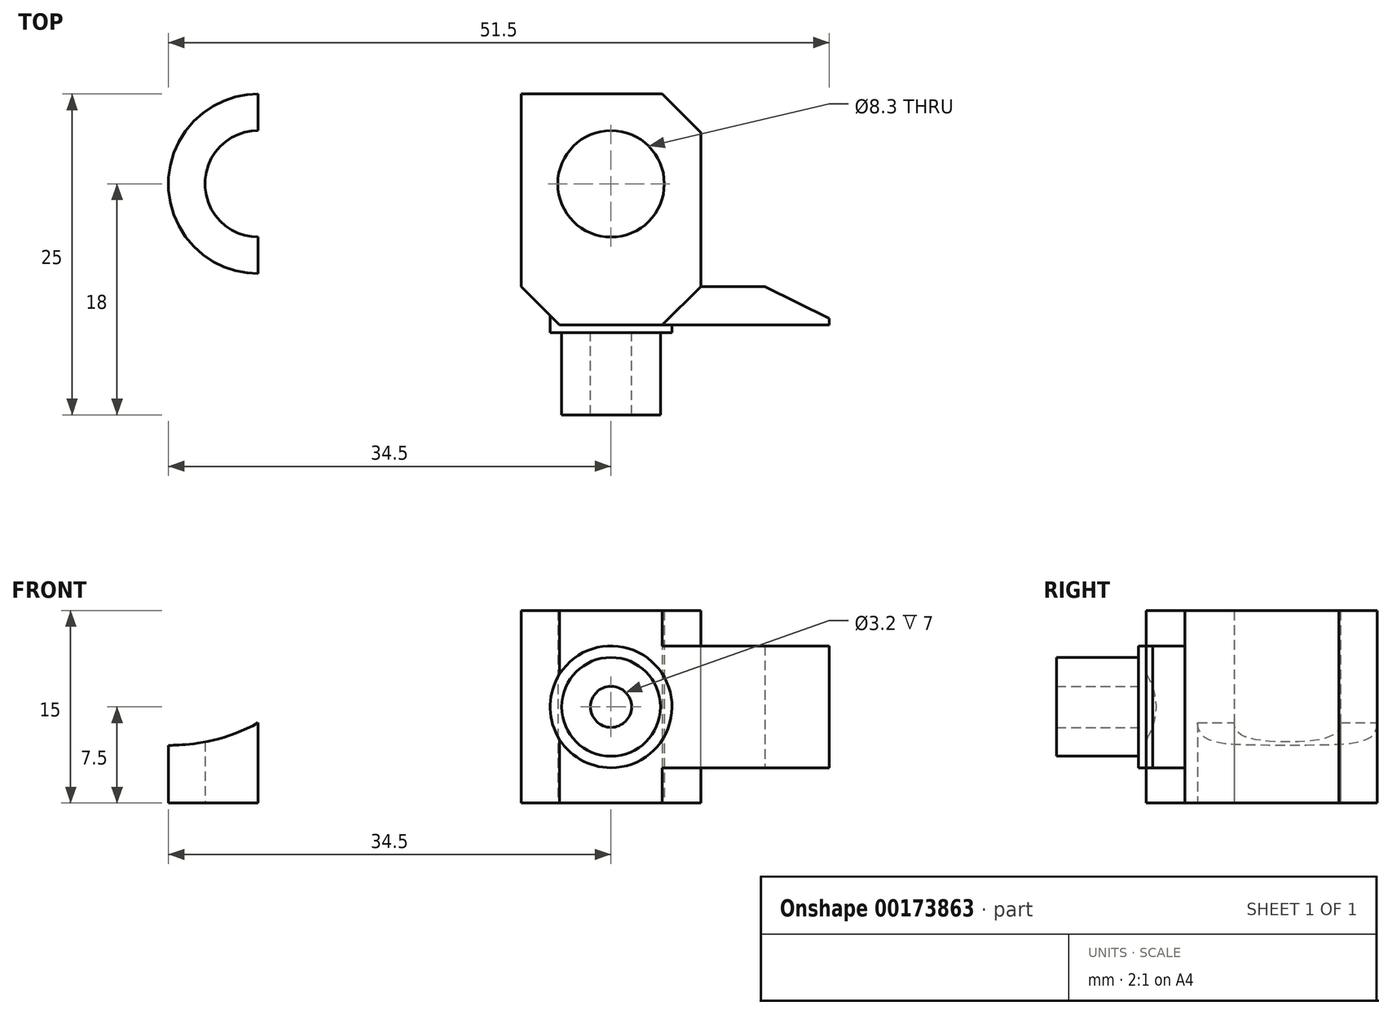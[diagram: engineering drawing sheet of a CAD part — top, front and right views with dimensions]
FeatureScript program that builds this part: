
annotation { "Feature Type Name" : "Feature", "Feature Type Description" : "" }
export const myFeature = defineFeature(function(context is Context, id is Id, definition is map)
    precondition{}
    {
        {
            var Q0;
            Q0=qCreatedBy(makeId("Top.planeOp"),FACE);
            var sketch = newSketch(context, id + "F0", { "sketchPlane" : qUnion([Q0])});
            skCircle(sketch, "E0", {"center": v(0, 0) * mm, "radius": 4.15 * mm});
            skLineSegment(sketch, "E1", {"start": v(0, 0) * mm, "end": v(-27.5, 0) * mm, "construction": true});
            skCircle(sketch, "E2", {"center": v(-27.5, 0) * mm, "radius": 4.15 * mm});
            skArc(sketch, "E3", {"start": v(-27.5, 7) * mm, "mid": v(-34.5, 0) * mm, "end": v(-27.5, -7) * mm});
            skLineSegment(sketch, "E4", {"start": v(-27.5, -7) * mm, "end": v(7, -7) * mm});
            skLineSegment(sketch, "E5", {"start": v(7, -7) * mm, "end": v(7, 7) * mm});
            skLineSegment(sketch, "E6", {"start": v(-27.5, 7) * mm, "end": v(7, 7) * mm});
            skSolve(sketch);
        }
        {
            var Q0;
            Q0=makeQuery(id+"F0.imprint","IMPRINT",FACE,{"disambiguationData":[TD([[makeQuery(id+"F0.imprint","IMPRINT",EDGE,{"derivedFrom":sQuery(id+"F0.wireOp",EDGE,"E0")}),-1.0]])]});
            extrude(context, id + "F1", {"entities" : qUnion([Q0]), "depth" : 15 * mm});
        }
        {
            var Q0;
            Q0=makeQuery(id+"F1.opExtrude","SWEPT_FACE",FACE,{"disambiguationData":[OSD([sQuery(id+"F0.wireOp",EDGE,"E4")])]});
            var sketch = newSketch(context, id + "F2", { "sketchPlane" : qUnion([Q0])});
            skLineSegment(sketch, "E7", {"start": v(-7, 15) * mm, "end": v(-7, 0) * mm});
            skSolve(sketch);
        }
        {
            var Q0;
            {var subQ0=sQuery(id+"F2.wireOp",EDGE,"E7");Q0=makeQuery(id+"F2.imprint","IMPRINT",FACE,{"disambiguationData":[TD([[makeQuery(id+"F2.imprint","IMPRINT",EDGE,{"derivedFrom":subQ0}),1.0]])]});}
            extrude(context, id + "F3", {"entities" : qUnion([Q0]), "operationType" : NewBodyOperationType.ADD, "depth" : 4 * mm});
        }
        {
            var Q0;
            Q0=makeQuery(id+"F3.opExtrude","CAP_FACE",FACE,{"disambiguationData":[OSD([sQuery(id+"F0.wireOp",EDGE,"E4"),sQuery(id+"F0.wireOp",EDGE,"E5"),sQuery(id+"F2.wireOp",EDGE,"E7")])],"isStart":false});
            var sketch = newSketch(context, id + "F4", { "sketchPlane" : qUnion([Q0])});
            skCircle(sketch, "E8", {"center": v(0, 7.5) * mm, "radius": 3.85 * mm});
            skCircle(sketch, "E9", {"center": v(0, 7.5) * mm, "radius": 1.6 * mm});
            skCircle(sketch, "E10", {"center": v(0, 7.5) * mm, "radius": 4.75 * mm});
            skPoint(sketch, "E11.positionSnap0", {"position": v(0, 15) * mm});
            skPoint(sketch, "E11.positionSnap1", {"position": v(7, 7.5) * mm});
            skLineSegment(sketch, "E12", {"start": v(0, 12.25) * mm, "end": v(-18, 12.25) * mm});
            skLineSegment(sketch, "E13", {"start": v(-18, 12.25) * mm, "end": v(-18, 2.75) * mm});
            skLineSegment(sketch, "E14", {"start": v(-18, 2.75) * mm, "end": v(0, 2.75) * mm});
            skLineSegment(sketch, "E15", {"start": v(0, 2.75) * mm, "end": v(18, 2.75) * mm});
            skLineSegment(sketch, "E16", {"start": v(18, 2.75) * mm, "end": v(18, 12.25) * mm});
            skLineSegment(sketch, "E17", {"start": v(18, 12.25) * mm, "end": v(0, 12.25) * mm});
            skSolve(sketch);
        }
        {
            var Q0;
            Q0 = qSketchRegion(id + "F4", true);
            extrude(context, id + "F5", {"entities" : qUnion([Q0]), "operationType" : NewBodyOperationType.ADD, "oppositeDirection" : true, "depth" : 3 * mm});
        }
        {
            var Q0;
            Q0=makeQuery(id+"F5.opExtrude","CAP_EDGE",EDGE,{"disambiguationData":[OSD([sQuery(id+"F4.wireOp",EDGE,"E13")])],"isStart":false});
            var Q1;
            Q1=makeQuery(id+"F5.opExtrude","CAP_EDGE",EDGE,{"disambiguationData":[OSD([sQuery(id+"F4.wireOp",EDGE,"E16")])],"isStart":false});
            chamfer(context, id + "F6", {"entities" : qUnion([Q0, Q1]), "chamferType" : ChamferType.TWO_OFFSETS, "width1" : 3 * mm, "oppositeDirection" : false, "width2" : 6 * mm, "tangentPropagation" : true});
        }
        {
            var Q0;
            Q0=makeQuery(id+"F4.imprint","IMPRINT",FACE,{"disambiguationData":[TD([[makeQuery(id+"F4.imprint","IMPRINT",EDGE,{"derivedFrom":sQuery(id+"F4.wireOp",EDGE,"E8")}),1.0]])]});
            extrude(context, id + "F7", {"entities" : qUnion([Q0]), "operationType" : NewBodyOperationType.ADD, "depth" : 7 * mm});
        }
        {
            var Q0;
            Q0=makeQuery(id+"F4.imprint","IMPRINT",FACE,{"disambiguationData":[TD([[makeQuery(id+"F4.imprint","IMPRINT",EDGE,{"derivedFrom":sQuery(id+"F4.wireOp",EDGE,"E8")}),-1.0]])]});
            extrude(context, id + "F8", {"entities" : qUnion([Q0]), "operationType" : NewBodyOperationType.ADD, "depth" : .6 * mm});
        }
        {
            var Q0;
            Q0=makeQuery(id+"F1.opExtrude","SWEPT_FACE",FACE,{"disambiguationData":[OSD([sQuery(id+"F0.wireOp",EDGE,"E4")])]});
            var sketch = newSketch(context, id + "F9", { "sketchPlane" : qUnion([Q0])});
            skLineSegment(sketch, "E18", {"start": v(-34.5, 0) * mm, "end": v(-34.5, 4.5) * mm});
            skLineSegment(sketch, "E19", {"start": v(0, 0) * mm, "end": v(17, 0) * mm});
            skLineSegment(sketch, "E20", {"start": v(17, 0) * mm, "end": v(17, 15) * mm});
            skLineSegment(sketch, "E21", {"start": v(17, 15) * mm, "end": v(-9, 15) * mm});
            skFitSpline(sketch, "E22", {"points": [v(-34.5, 4.5) * mm, v(-9, 15) * mm], "startDerivative": vector(34.5, 0.37) * mm, "endDerivative": vector(41.77, 0) * mm});
            skLineSegment(sketch, "E23", {"start": v(0, 0) * mm, "end": v(-34.5, 0) * mm});
            skSolve(sketch);
        }
        {
            var Q0;
            {var subQ0=makeQuery(id+"F3.opExtrude","CAP_EDGE",EDGE,{"disambiguationData":[OSD([sQuery(id+"F2.wireOp",EDGE,"E7")])],"isStart":true});Q0=makeQuery(id+"F9.imprint","IMPRINT",FACE,{"disambiguationData":[TD([[makeQuery(id+"F9.imprint","IMPRINT",EDGE,{"derivedFrom":subQ0}),-1.0]])]});}
            var Q1;
            {var subQ0=sQuery(id+"F9.wireOp",EDGE,"E18");Q1=makeQuery(id+"F9.imprint","IMPRINT",FACE,{"disambiguationData":[TD([[makeQuery(id+"F9.imprint","IMPRINT",EDGE,{"derivedFrom":subQ0}),-1.0]])]});}
            var Q2;
            {var subQ2=sQuery(id+"F9.wireOp",EDGE,"E19");Q2=makeQuery(id+"F9.imprint","IMPRINT",FACE,{"disambiguationData":[TD([[makeQuery(id+"F9.imprint","IMPRINT",EDGE,{"derivedFrom":subQ2}),1.0]])]});}
            extrude(context, id + "F10", {"entities" : qUnion([Q0, Q1, Q2]), "operationType" : NewBodyOperationType.INTERSECT, "endBound" : BoundingType.SYMMETRIC, "depth" : 50 * mm});
        }
        {
            var Q0;
            Q0=makeQuery(id+"F3.opExtrude","CAP_EDGE",EDGE,{"disambiguationData":[OSD([sQuery(id+"F0.wireOp",EDGE,"E4"),sQuery(id+"F0.wireOp",EDGE,"E5")])],"isStart":false});
            var Q1;
            Q1=makeQuery(id+"F1.opExtrude","SWEPT_EDGE",EDGE,{"disambiguationData":[OSD([sQuery(id+"F0.wireOp",EDGE,"E5"),sQuery(id+"F0.wireOp",EDGE,"E6")])]});
            var Q2;
            {var subQ3=sQuery(id+"F2.wireOp",EDGE,"E7");var subQ4=sQuery(id+"F4.wireOp",EDGE,"E17");var subQ5=sQuery(id+"F4.wireOp",EDGE,"E12");Q2=makeQuery(id+"F5.boolean.opBoolean","SPLIT",EDGE,{"disambiguationData":[TD([makeQuery(id+"F5.opExtrude","SWEPT_FACE",FACE,{"disambiguationData":[OSD([subQ5,subQ4])]})])],"derivedFrom":makeQuery(id+"F3.opExtrude","CAP_EDGE",EDGE,{"disambiguationData":[OSD([subQ3])],"isStart":false})});}
            var Q3;
            {var subQ3=sQuery(id+"F2.wireOp",EDGE,"E7");var subQ4=sQuery(id+"F4.wireOp",EDGE,"E15");var subQ5=sQuery(id+"F4.wireOp",EDGE,"E14");Q3=makeQuery(id+"F5.boolean.opBoolean","SPLIT",EDGE,{"disambiguationData":[TD([makeQuery(id+"F5.opExtrude","SWEPT_FACE",FACE,{"disambiguationData":[OSD([subQ5,subQ4])]})])],"derivedFrom":makeQuery(id+"F3.opExtrude","CAP_EDGE",EDGE,{"disambiguationData":[OSD([subQ3])],"isStart":false})});}
            chamfer(context, id + "F11", {"entities" : qUnion([Q0, Q1, Q2, Q3]), "width" : 3 * mm, "tangentPropagation" : true});
        }
    });
